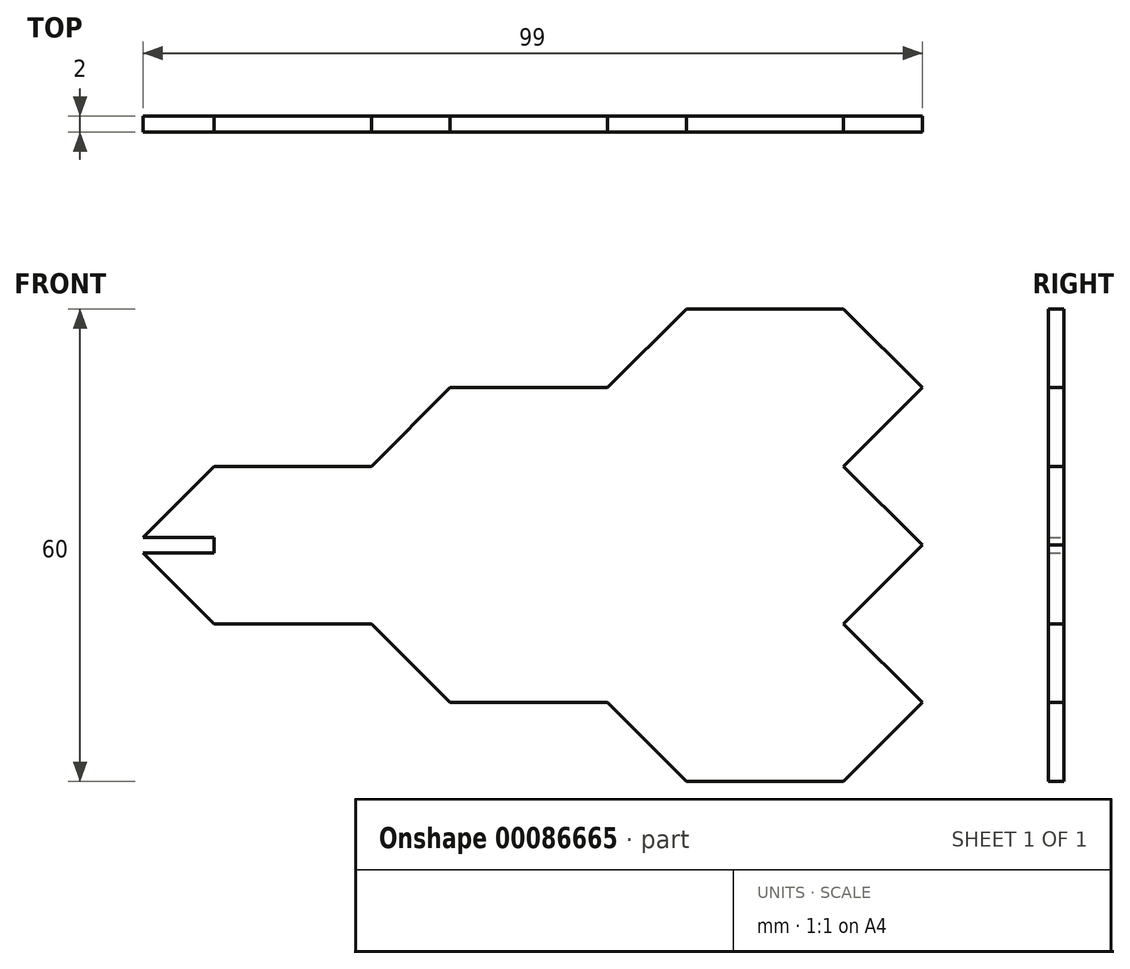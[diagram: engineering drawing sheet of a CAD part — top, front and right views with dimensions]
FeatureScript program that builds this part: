
annotation { "Feature Type Name" : "Feature", "Feature Type Description" : "" }
export const myFeature = defineFeature(function(context is Context, id is Id, definition is map)
    precondition{}
    {
        {
            var Q0;
            Q0=qCreatedBy(makeId("Front.planeOp"),FACE);
            var sketch = newSketch(context, id + "F0", { "sketchPlane" : qUnion([Q0])});
            skLineSegment(sketch, "E0", {"start": v(0, 0) * mm, "end": v(0, 1) * mm});
            skLineSegment(sketch, "E1", {"start": v(0, 1) * mm, "end": v(-9, 1) * mm});
            skLineSegment(sketch, "E2", {"start": v(-9, 1) * mm, "end": v(0, 10) * mm});
            skLineSegment(sketch, "E3", {"start": v(0, 10) * mm, "end": v(20, 10) * mm});
            skLineSegment(sketch, "E4", {"start": v(20, 10) * mm, "end": v(30, 20) * mm});
            skLineSegment(sketch, "E5", {"start": v(30, 20) * mm, "end": v(50, 20) * mm});
            skLineSegment(sketch, "E6", {"start": v(50, 20) * mm, "end": v(60, 30) * mm});
            skLineSegment(sketch, "E7", {"start": v(60, 30) * mm, "end": v(80, 30) * mm});
            skLineSegment(sketch, "E8", {"start": v(80, 30) * mm, "end": v(90, 20) * mm});
            skLineSegment(sketch, "E9", {"start": v(90, 20) * mm, "end": v(80, 10) * mm});
            skLineSegment(sketch, "E10", {"start": v(80, 10) * mm, "end": v(90, 0) * mm});
            skLineSegment(sketch, "E11", {"start": v(90, 0) * mm, "end": v(80, -10) * mm});
            skLineSegment(sketch, "E12", {"start": v(80, -10) * mm, "end": v(90, -20) * mm});
            skLineSegment(sketch, "E13", {"start": v(90, -20) * mm, "end": v(80, -30) * mm});
            skLineSegment(sketch, "E14", {"start": v(80, -30) * mm, "end": v(60, -30) * mm});
            skLineSegment(sketch, "E15", {"start": v(60, -30) * mm, "end": v(50, -20) * mm});
            skLineSegment(sketch, "E16", {"start": v(50, -20) * mm, "end": v(30, -20) * mm});
            skLineSegment(sketch, "E17", {"start": v(30, -20) * mm, "end": v(20, -10) * mm});
            skLineSegment(sketch, "E18", {"start": v(20, -10) * mm, "end": v(0, -10) * mm});
            skLineSegment(sketch, "E19", {"start": v(0, -10) * mm, "end": v(-9, -1) * mm});
            skLineSegment(sketch, "E20", {"start": v(-9, -1) * mm, "end": v(0, -1) * mm});
            skLineSegment(sketch, "E21", {"start": v(0, -1) * mm, "end": v(0, 0) * mm});
            skSolve(sketch);
        }
        {
            var Q0;
            Q0=makeQuery(id+"F0.imprint","IMPRINT",FACE,{"disambiguationData":[TD([[makeQuery(id+"F0.imprint","IMPRINT",EDGE,{"derivedFrom":sQuery(id+"F0.wireOp",EDGE,"E0")}),-1.0]])]});
            extrude(context, id + "F1", {"entities" : qUnion([Q0]), "depth" : 1 * mm, "hasSecondDirection" : true, "secondDirectionOppositeDirection" : true, "secondDirectionDepth" : 1 * mm});
        }
    });
